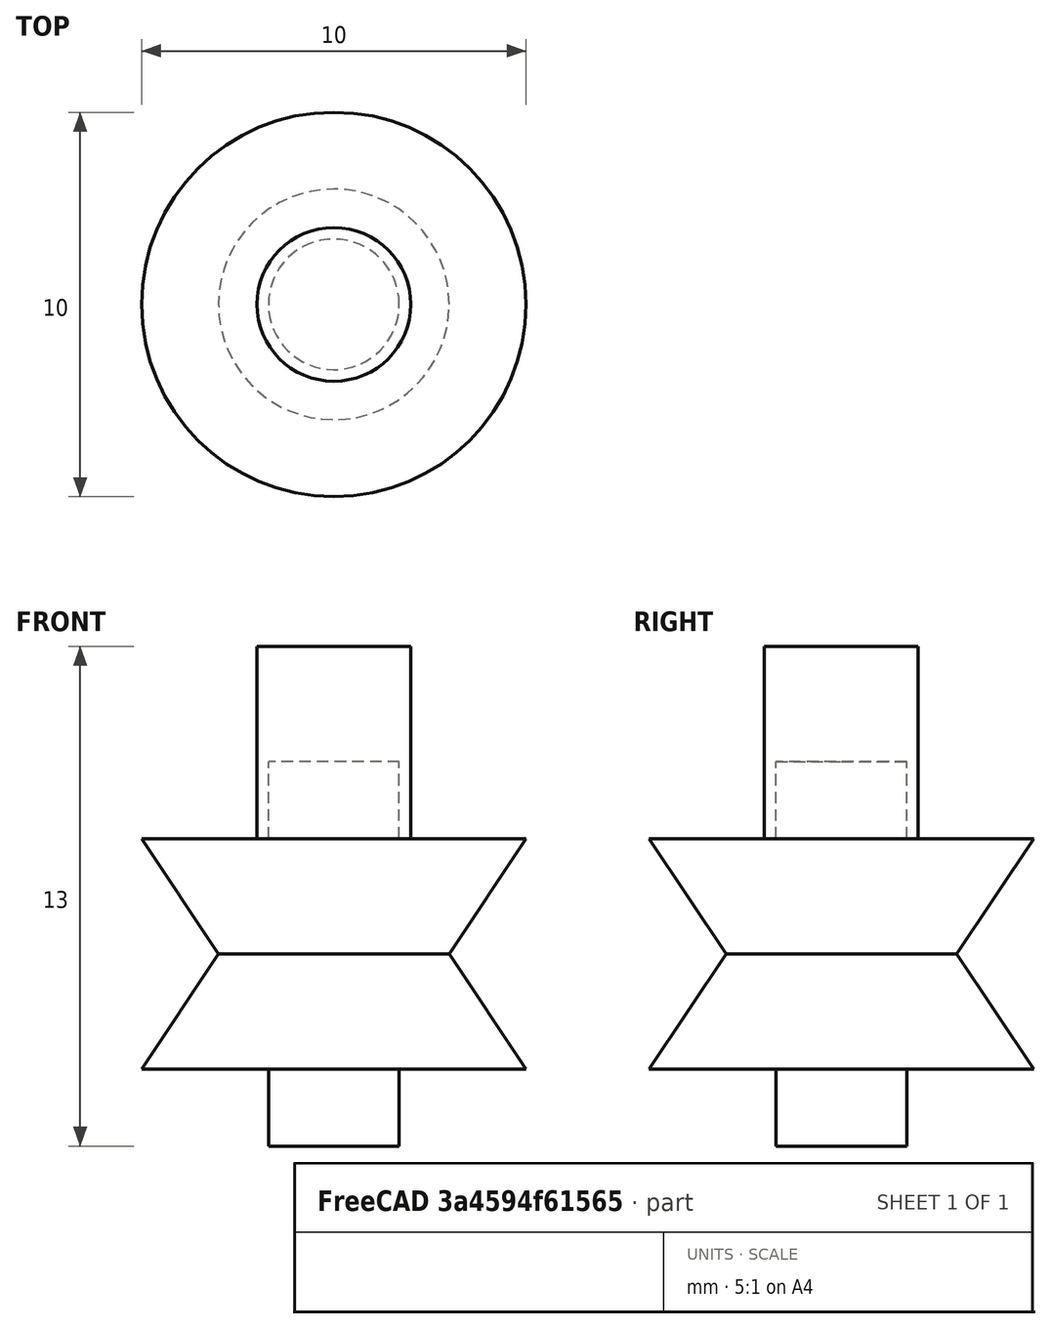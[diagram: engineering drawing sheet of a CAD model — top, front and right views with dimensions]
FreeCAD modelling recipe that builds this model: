
FCSTD DOCUMENT  (FreeCAD 0.16R6706 (Git))
Label: Prueba cilindros modulo tensionador
License: All rights reserved
LicenseURL: http://en.wikipedia.org/wiki/All_rights_reserved
objects: Part::Cone×2, Part::Fuse×2, Part::Feature×2, Part::MultiFuse×1, Part::Cylinder×1, Part::Cut×1
note: 9 computed .brp shape members not serialized (recipe doc carries the construction recipe); baked Part::Feature solids carry a one-line shape summary decoded from their .brp

FEATURE [Part::Cone] Cone  label="Cono"
  Angle = 360
  Height = 3
  Radius1 = 3
  Radius2 = 5
FEATURE [Part::Cone] Cone001  label="Cono001"
  Angle = 360
  Height = 3
  Placement = pos=(0,0,0) rot=(1,0,0;3.14159rad)
  Radius1 = 3
  Radius2 = 5
FEATURE [Part::MultiFuse] Fusion
  Shapes = -> [Cone001,Cone]
FEATURE [Part::Cylinder] Cylinder  label="Cilindro"
  Angle = 360
  Height = 10
  Placement = pos=(0,0,-5) rot=(0,0,1;0rad)
  Radius = 1.7
FEATURE [Part::Fuse] Fusion001
  Base = -> Cylinder
  Tool = -> Fusion
FEATURE [Part::Feature] Fusion001001  label="Fusion002"
  shape: bbox 10 x 10 x 11 mm, 6 faces (baked)
FEATURE [Part::Fuse] Fusion001002
  Base = -> Cylinder
  Tool = -> Fusion
FEATURE [Part::Feature] Fusion001002001  label="Fusion001003"
  shape: bbox 10 x 10 x 11 mm, 6 faces (baked)
FEATURE [Part::Cut] Cut  label="tensioner"
  Base = -> Fusion
  Tool = -> Cylinder
